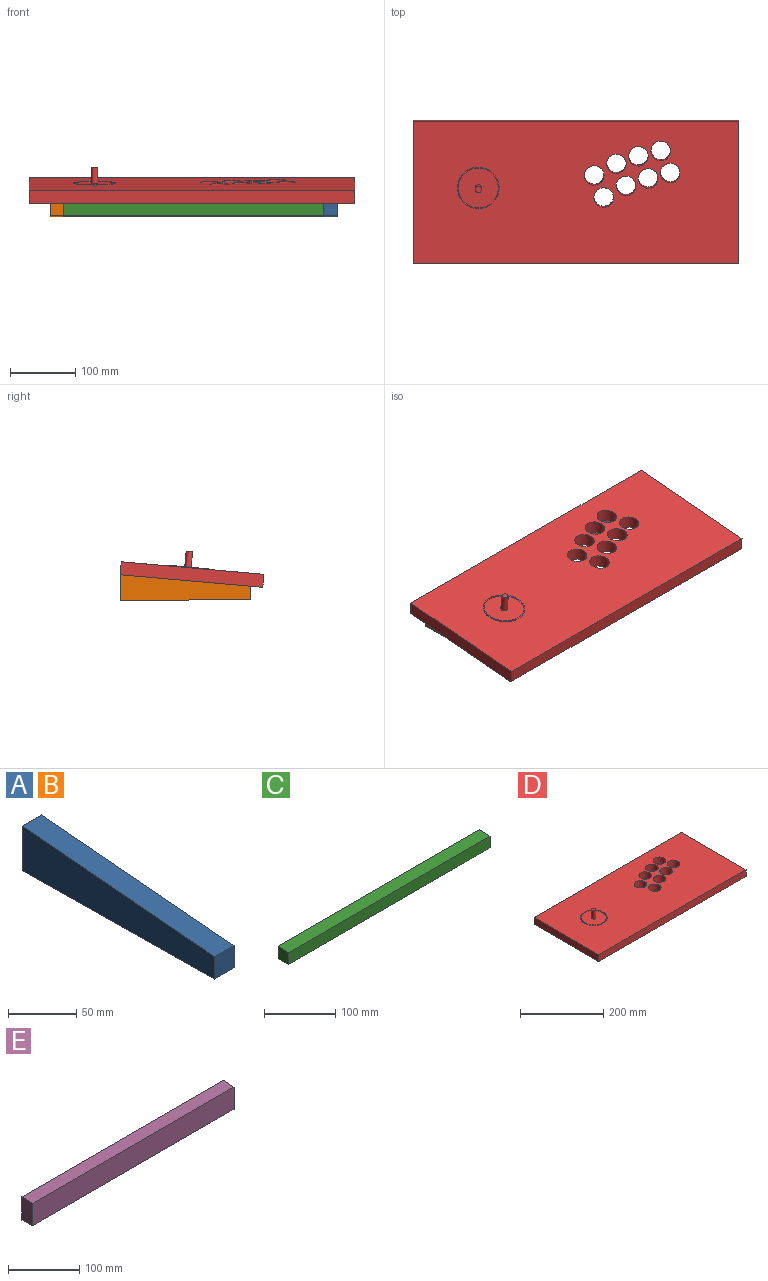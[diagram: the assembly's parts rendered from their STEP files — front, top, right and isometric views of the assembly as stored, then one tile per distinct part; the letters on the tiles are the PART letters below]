
ASSEMBLY  parts=5 mates=8
PART A: 6 faces, bbox 20x200x40 mm
  f0: plane 199.98x20mm, normal (0,-0.09,1), area 4015mm2, adj f1,f3,f4,f5
  f1: plane 20x20mm, normal (0,-1,0), area 400mm2, adj f0,f2,f4,f5
  f2: plane 199.98x20mm, normal (0,-0.01,-1), area 4000mm2, adj f1,f3,f4,f5
  f3: plane 40x20mm, normal (0,1,0), area 800mm2, adj f0,f2,f4,f5
  f4: plane 199.98x40mm, normal (1,0,0), area 5999.5mm2, adj f0,f1,f2,f3
  f5: plane 199.98x40mm, normal (-1,0,0), area 5999.5mm2, adj f0,f1,f2,f3
PART B: same geometry as A
PART C: 6 faces, bbox 400x20x22 mm
  f0: plane 400x20mm, normal (0,-0.09,1), area 8029.9mm2, adj f1,f3,f4,f5
  f1: plane 400x20mm, normal (0,-1,0), area 8000mm2, adj f0,f2,f4,f5
  f2: plane 400x20mm, normal (0,-0.01,-1), area 8000mm2, adj f1,f3,f4,f5
  f3: plane 400x22mm, normal (0,1,0), area 8800mm2, adj f0,f2,f4,f5
  f4: plane 22x20mm, normal (1,0,0), area 420mm2, adj f0,f1,f2,f3
  f5: plane 22x20mm, normal (-1,0,0), area 420mm2, adj f0,f1,f2,f3
PART D: 20 faces, bbox 500x220x45 mm
  f0: plane 220x20mm, normal (-1,0,0), area 4400mm2, adj f1,f11,f12,f13
  f1: plane 500x20mm, normal (0,-1,0), area 10000mm2, adj f0,f2,f12,f13
  f2: plane 220x20mm, normal (1,0,0), area 4400mm2, adj f1,f11,f12,f13
  f3: cylinder r=15mm len=30mm, axis (0,0,-1), area 1885mm2, adj f12,f13
  f4: cylinder r=15mm len=30mm, axis (0,0,-1), area 1885mm2, adj f12,f13
  f5: cylinder r=15mm len=30mm, axis (0,0,-1), area 1885mm2, adj f12,f13
  f6: cylinder r=15mm len=30mm, axis (0,0,-1), area 1885mm2, adj f12,f13
  f7: cylinder r=15mm len=30mm, axis (0,0,-1), area 1885mm2, adj f12,f13
  f8: cylinder r=15mm len=30mm, axis (0,0,-1), area 1885mm2, adj f12,f13
  f9: cylinder r=15mm len=30mm, axis (0,0,-1), area 1885mm2, adj f12,f13
  f10: cylinder r=15mm len=30mm, axis (0,0,-1), area 1885mm2, adj f12,f13
  f11: plane 500x20mm, normal (0,1,0), area 10000mm2, adj f0,f2,f12,f13
  f12: plane 500x220mm, normal (0,0,1), area 101128.1mm2, adj f0,f1,f2,f3,f4,f5,f6,f7
  f13: plane 500x220mm, normal (0,0,-1), area 104345.1mm2, adj f0,f1,f2,f3,f4,f5,f6,f7
  f14: cylinder r=30.75mm len=61.5mm, axis (0,0,-1), area 193.2mm2, adj f16,f17
  f15: cylinder r=32mm len=64mm, axis (0,0,-1), area 201.1mm2, adj f12,f16
  f16: plane 64x64mm, normal (0,0,1), area 246.4mm2, adj f14,f15
  f17: plane 61.5x61.5mm, normal (0,0,1), area 2892mm2, adj f14,f18
  f18: cylinder r=5mm len=25mm, axis (0,0,-1), area 785.4mm2, adj f17,f19
  f19: plane 10x10mm, normal (0,0,1), area 78.5mm2, adj f18
PART E: 6 faces, bbox 400x20x40 mm
  f0: plane 400x40mm, normal (0,1,0), area 16000mm2, adj f1,f3,f4,f5
  f1: plane 400x20mm, normal (0,-0.09,1), area 8029.9mm2, adj f0,f2,f4,f5
  f2: plane 400x38mm, normal (0,-1,0), area 15200mm2, adj f1,f3,f4,f5
  f3: plane 400x20mm, normal (0,-0.01,-1), area 8000mm2, adj f0,f2,f4,f5
  f4: plane 40x20mm, normal (1,0,0), area 779.9mm2, adj f0,f1,f2,f3
  f5: plane 40x20mm, normal (-1,0,0), area 779.9mm2, adj f0,f1,f2,f3
PLACE A t=(266.32,44.1,-66.23)mm
PLACE B t=(-153.68,44.09,-66.23)mm
PLACE C t=(-143.68,30.47,-70.86)mm
PLACE D rot(axis=(1,0,0),5deg) t=(19.2,40.47,-50.98)mm
PLACE E t=(-143.68,29.35,-70.85)mm
MATE parallel B.f2 <-> E.f3  axis (0,-0.01,-1) through (-153.68,27.86,-82.08)mm
MATE planar A.f5 <-> C.f4  axis (-1,0,0) through (256.32,38.97,-66.67)mm
MATE planar D.f13 <-> A.f0  axis (0,0.09,-1) through (48.99,17.09,-53.03)mm
MATE planar A.f5 <-> E.f4  axis (-1,0,0) through (256.32,38.97,-66.67)mm
MATE planar B.f4 <-> E.f5  axis (1,0,0) through (-143.68,38.97,-66.67)mm
MATE planar B.f4 <-> C.f5  axis (1,0,0) through (-143.68,38.97,-66.67)mm
MATE planar A.f2 <-> E.f3  axis (0,-0.01,-1) through (266.32,27.86,-82.08)mm
MATE planar B.f2 <-> A.f2  axis (0,-0.01,-1) through (-153.68,27.86,-82.08)mm
